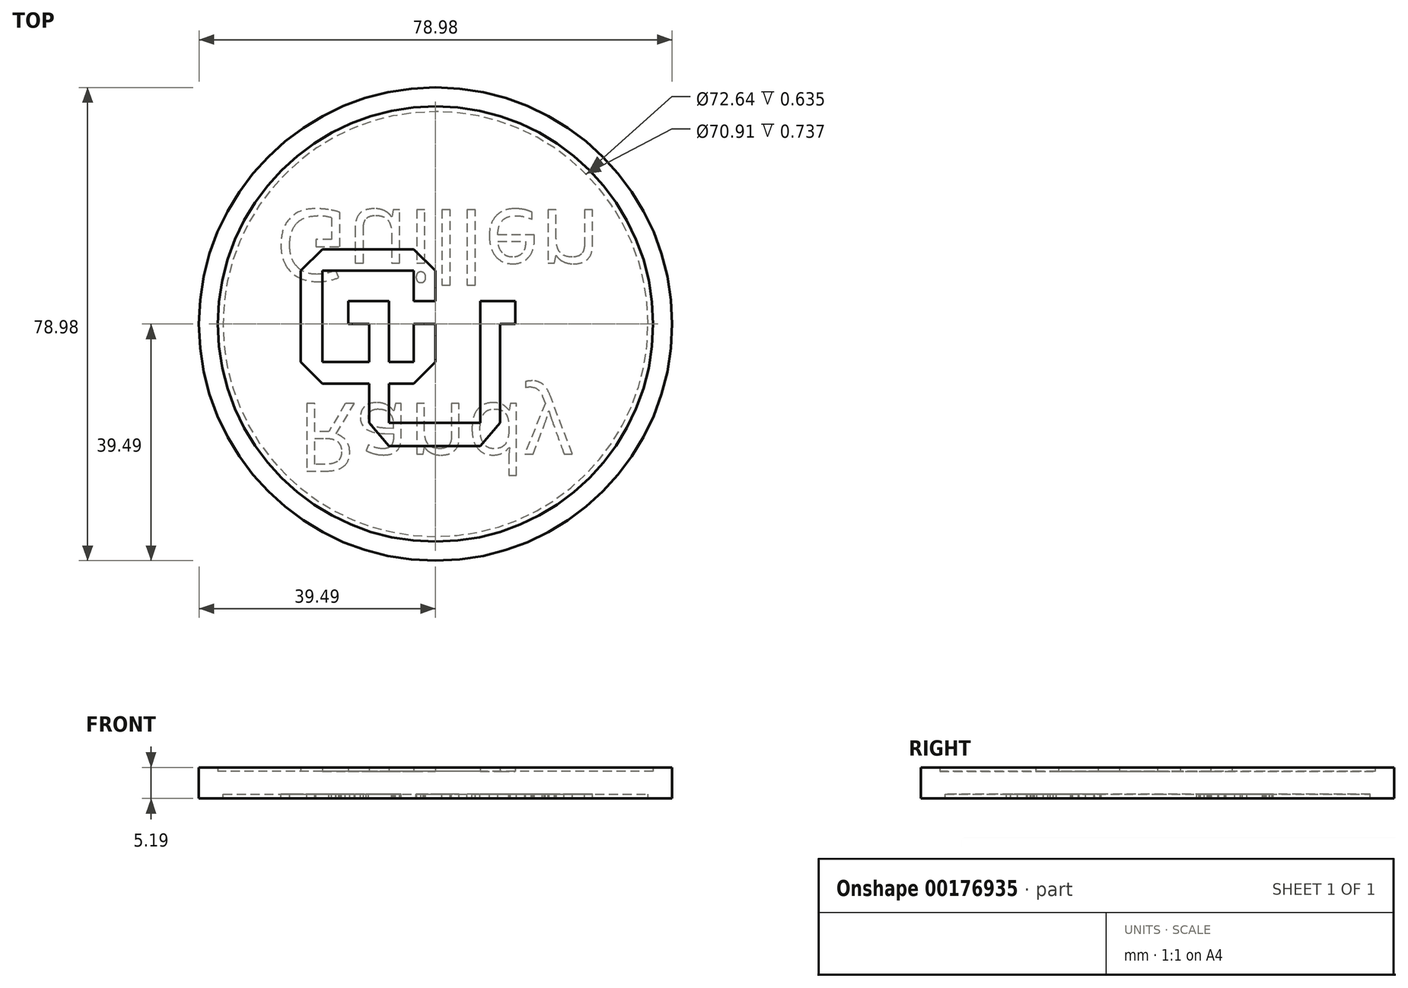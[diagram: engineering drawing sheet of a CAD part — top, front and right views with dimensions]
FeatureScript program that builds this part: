
annotation { "Feature Type Name" : "Feature", "Feature Type Description" : "" }
export const myFeature = defineFeature(function(context is Context, id is Id, definition is map)
    precondition{}
    {
        {
            var Q0;
            Q0=qCreatedBy(makeId("Top.planeOp"),FACE);
            var sketch = newSketch(context, id + "F0", { "sketchPlane" : qUnion([Q0])});
            skCircle(sketch, "E0", {"center": v(0, 0) * mm, "radius": 39.5 * mm});
            skSolve(sketch);
        }
        {
            var Q0;
            Q0=makeQuery(id+"F0.imprint","IMPRINT",FACE,{"disambiguationData":[TD([[makeQuery(id+"F0.imprint","IMPRINT",EDGE,{"derivedFrom":sQuery(id+"F0.wireOp",EDGE,"E0")}),1.0]])]});
            extrude(context, id + "F1", {"entities" : qUnion([Q0]), "depth" : 3.8 * mm});
        }
        {
            var Q0;
            Q0=makeQuery(id+"F1.opExtrude","CAP_FACE",FACE,{"disambiguationData":[OSD([sQuery(id+"F0.wireOp",EDGE,"E0")])],"isStart":false});
            var sketch = newSketch(context, id + "F2", { "sketchPlane" : qUnion([Q0])});
            skLineSegment(sketch, "E1", {"start": v(0, 0) * mm, "end": v(0, -6.35) * mm});
            skLineSegment(sketch, "E2", {"start": v(0, -6.35) * mm, "end": v(-3.62, -9.9) * mm});
            skLineSegment(sketch, "E3", {"start": v(-3.62, -9.9) * mm, "end": v(-7.77, -9.9) * mm});
            skLineSegment(sketch, "E4", {"start": v(-18.86, -9.9) * mm, "end": v(-22.49, -6.35) * mm});
            skLineSegment(sketch, "E5", {"start": v(-22.49, -6.35) * mm, "end": v(-22.49, 8.89) * mm});
            skLineSegment(sketch, "E6", {"start": v(-22.49, 8.89) * mm, "end": v(-18.86, 12.45) * mm});
            skLineSegment(sketch, "E7", {"start": v(-18.86, 12.45) * mm, "end": v(-3.62, 12.45) * mm});
            skLineSegment(sketch, "E8", {"start": v(-3.62, 12.45) * mm, "end": v(0, 8.9) * mm});
            skLineSegment(sketch, "E9", {"start": v(0, 8.9) * mm, "end": v(0, 3.81) * mm});
            skLineSegment(sketch, "E10", {"start": v(0, 3.81) * mm, "end": v(-3.62, 3.81) * mm});
            skLineSegment(sketch, "E11", {"start": v(-3.62, 3.8) * mm, "end": v(-3.62, 8.9) * mm});
            skLineSegment(sketch, "E12", {"start": v(-3.62, 8.9) * mm, "end": v(-18.86, 8.89) * mm});
            skLineSegment(sketch, "E13", {"start": v(-18.86, 8.89) * mm, "end": v(-18.86, -6.35) * mm});
            skLineSegment(sketch, "E14", {"start": v(-18.86, -6.35) * mm, "end": v(-11.08, -6.35) * mm});
            skLineSegment(sketch, "E15", {"start": v(-3.62, -6.35) * mm, "end": v(-3.62, 0) * mm});
            skLineSegment(sketch, "E16", {"start": v(-3.62, 0) * mm, "end": v(0, 0) * mm});
            skLineSegment(sketch, "E17", {"start": v(-7.77, -6.35) * mm, "end": v(-7.77, 3.8) * mm});
            skLineSegment(sketch, "E18", {"start": v(-7.77, 3.81) * mm, "end": v(-14.57, 3.8) * mm});
            skLineSegment(sketch, "E19", {"start": v(-14.57, 3.81) * mm, "end": v(-14.57, 0) * mm});
            skLineSegment(sketch, "E20", {"start": v(-14.57, 0) * mm, "end": v(-11.08, 0) * mm});
            skLineSegment(sketch, "E21", {"start": v(-11.08, 0) * mm, "end": v(-11.08, -6.35) * mm});
            skLineSegment(sketch, "E22.trimOffspring", {"start": v(-7.77, -6.35) * mm, "end": v(-3.62, -6.35) * mm});
            skLineSegment(sketch, "E23", {"start": v(-11.08, -9.9) * mm, "end": v(-11.08, -16.51) * mm});
            skLineSegment(sketch, "E24", {"start": v(-11.08, -16.51) * mm, "end": v(-7.77, -20.37) * mm});
            skLineSegment(sketch, "E25", {"start": v(-7.77, -20.37) * mm, "end": v(7.47, -20.37) * mm});
            skLineSegment(sketch, "E26", {"start": v(7.47, -20.37) * mm, "end": v(10.78, -16.51) * mm});
            skLineSegment(sketch, "E27", {"start": v(10.78, -16.51) * mm, "end": v(10.78, 0) * mm});
            skLineSegment(sketch, "E28", {"start": v(10.78, 0) * mm, "end": v(13.32, 0) * mm});
            skLineSegment(sketch, "E29", {"start": v(13.32, 0) * mm, "end": v(13.32, 3.81) * mm});
            skLineSegment(sketch, "E30", {"start": v(13.32, 3.81) * mm, "end": v(7.47, 3.81) * mm});
            skLineSegment(sketch, "E31", {"start": v(7.47, 3.81) * mm, "end": v(7.47, -16.51) * mm});
            skLineSegment(sketch, "E32", {"start": v(7.47, -16.51) * mm, "end": v(-7.77, -16.51) * mm});
            skLineSegment(sketch, "E33", {"start": v(-7.77, -16.51) * mm, "end": v(-7.77, -9.9) * mm});
            skCircle(sketch, "E34", {"center": v(0, 0) * mm, "radius": 36.32 * mm});
            skLineSegment(sketch, "E35.trimOffspring", {"start": v(-11.08, -9.9) * mm, "end": v(-18.86, -9.9) * mm});
            skSolve(sketch);
        }
        {
            var Q0;
            Q0=makeQuery(id+"F2.imprint","IMPRINT",FACE,{"disambiguationData":[TD([[makeQuery(id+"F2.imprint","IMPRINT",EDGE,{"derivedFrom":sQuery(id+"F2.wireOp",EDGE,"E1")}),-1.0]])]});
            var Q1;
            Q1=makeQuery(id+"F2.imprint","IMPRINT",FACE,{"disambiguationData":[TD([[makeQuery(id+"F2.imprint","IMPRINT",EDGE,{"derivedFrom":sQuery(id+"F2.wireOp",EDGE,"E34")}),-1.0]])]});
            extrude(context, id + "F3", {"entities" : qUnion([Q0, Q1]), "operationType" : NewBodyOperationType.ADD, "depth" : 0.64 * mm});
        }
        {
            var Q0;
            Q0=makeQuery(id+"F1.opExtrude","CAP_FACE",FACE,{"disambiguationData":[OSD([sQuery(id+"F0.wireOp",EDGE,"E0")])],"isStart":true});
            var sketch = newSketch(context, id + "F4", { "sketchPlane" : qUnion([Q0])});
            skCircle(sketch, "E36", {"center": v(0, 0) * mm, "radius": 35.46 * mm});
            skSolve(sketch);
        }
        {
            var Q0;
            Q0=makeQuery(id+"F4.imprint","IMPRINT",FACE,{"disambiguationData":[TD([[makeQuery(id+"F4.imprint","IMPRINT",EDGE,{"derivedFrom":makeQuery(id+"F1.opExtrude","CAP_EDGE",EDGE,{"disambiguationData":[OSD([sQuery(id+"F0.wireOp",EDGE,"E0")])],"isStart":true})}),-1.0]])]});
            var sketch = newSketch(context, id + "F5", { "sketchPlane" : qUnion([Q0])});
            skText(sketch, "E37", { "text": "Randy ", "fontName": "OpenSans-Regular.ttf"});
            skText(sketch, "E38", { "text": "Guillen", "fontName": "OpenSans-Regular.ttf"});
            const initialGuessF5  = {"E37": [-0.02303, 0.01326, 1, 0, 0.01137], "E38": [-0.02682, -0.0191, 1, 0, 0.01195]};
            skSetInitialGuess(sketch, initialGuessF5);
            skSolve(sketch);
        }
        {
            var Q0;
            Q0 = qSketchRegion(id + "F5", true);
            var Q1;
            Q1=makeQuery(id+"F4.imprint","IMPRINT",FACE,{"disambiguationData":[TD([[makeQuery(id+"F4.imprint","IMPRINT",EDGE,{"derivedFrom":sQuery(id+"F4.wireOp",EDGE,"E36")}),-1.0]])]});
            extrude(context, id + "F6", {"entities" : qUnion([Q0, Q1]), "operationType" : NewBodyOperationType.ADD, "depth" : 0.74 * mm});
        }
    });
